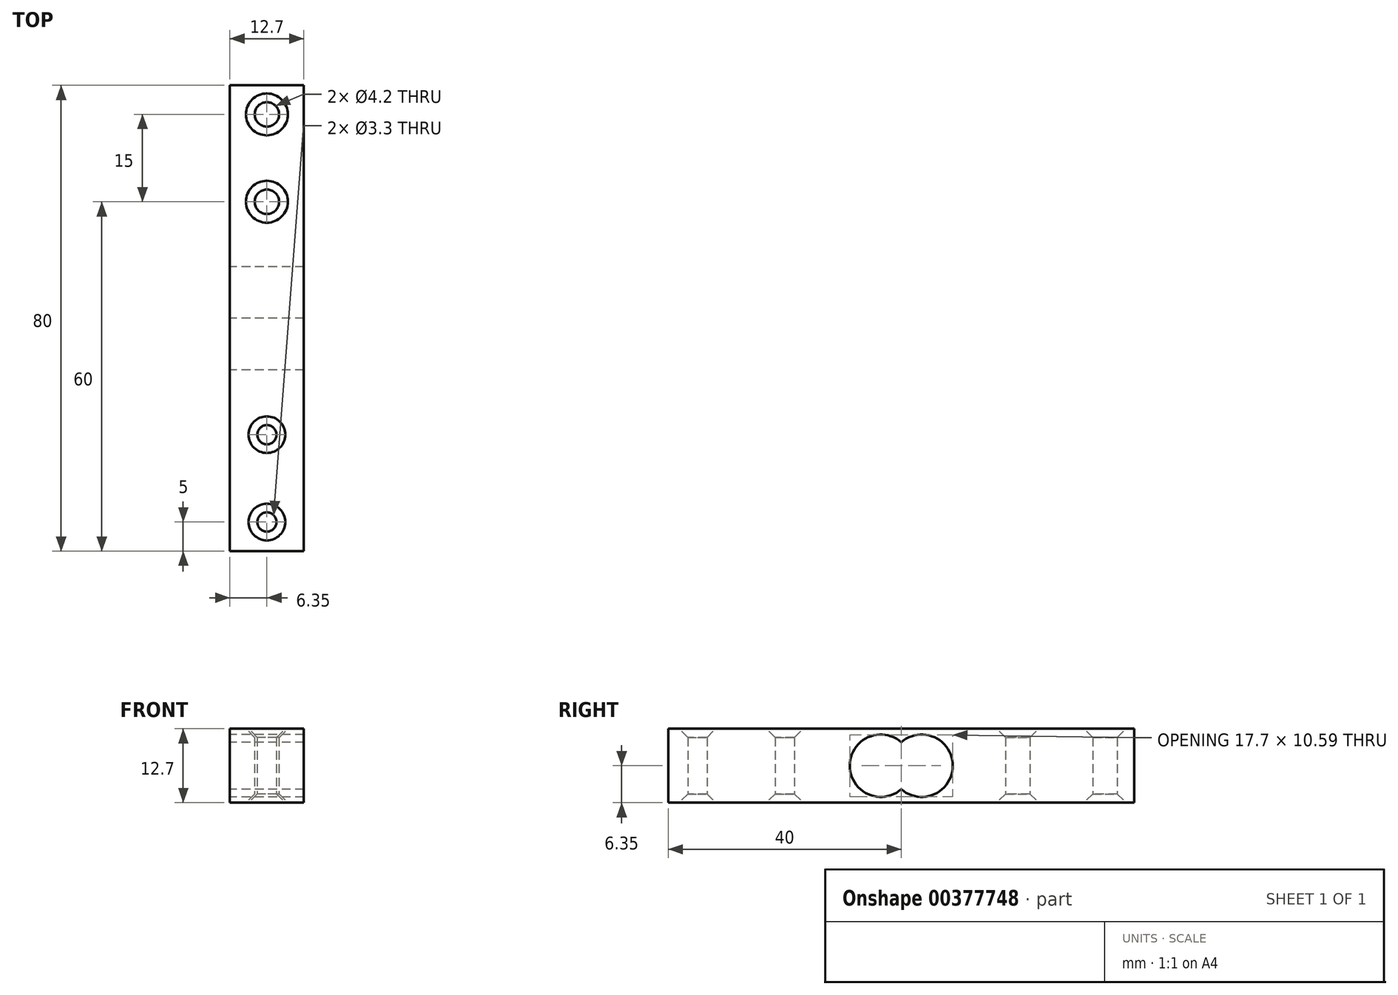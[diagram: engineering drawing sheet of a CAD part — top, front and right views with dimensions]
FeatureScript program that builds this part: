
annotation { "Feature Type Name" : "Feature", "Feature Type Description" : "" }
export const myFeature = defineFeature(function(context is Context, id is Id, definition is map)
    precondition{}
    {
        {
            var Q0;
            Q0=qCreatedBy(makeId("Top.planeOp"),FACE);
            var sketch = newSketch(context, id + "F0", { "sketchPlane" : qUnion([Q0])});
            skLineSegment(sketch, "E0.bottom", {"start": v(6.35, -40) * mm, "end": v(-6.35, -40) * mm});
            skLineSegment(sketch, "E0.top", {"start": v(6.35, 40) * mm, "end": v(-6.35, 40) * mm});
            skLineSegment(sketch, "E0.left", {"start": v(6.35, -40) * mm, "end": v(6.35, 40) * mm});
            skLineSegment(sketch, "E0.right", {"start": v(-6.35, -40) * mm, "end": v(-6.35, 40) * mm});
            skPoint(sketch, "E0.middle", {"position": v(0, 0) * mm});
            skLineSegment(sketch, "E1", {"start": v(0, 0) * mm, "end": v(0, 20) * mm, "construction": true});
            skLineSegment(sketch, "E2.MirrorCS", {"start": v(0, 0) * mm, "end": v(0, -20) * mm, "construction": true});
            skLineSegment(sketch, "E3", {"start": v(0, 20) * mm, "end": v(0, 35) * mm, "construction": true});
            skLineSegment(sketch, "E4.MirrorCS", {"start": v(0, -20) * mm, "end": v(0, -35) * mm, "construction": true});
            skCircle(sketch, "E5", {"center": v(0, 20) * mm, "radius": 2.1 * mm});
            skCircle(sketch, "E6", {"center": v(0, 35) * mm, "radius": 2.1 * mm});
            skCircle(sketch, "E7", {"center": v(0, -20) * mm, "radius": 1.65 * mm});
            skCircle(sketch, "E8", {"center": v(0, -35) * mm, "radius": 1.65 * mm});
            skSolve(sketch);
        }
        {
            var Q0;
            Q0 = qSketchRegion(id + "F0", true);
            extrude(context, id + "F1", {"entities" : qUnion([Q0]), "depth" : 12.7 * mm});
        }
        {
            var Q0;
            Q0=makeQuery(id+"F1.opExtrude","SWEPT_FACE",FACE,{"disambiguationData":[OSD([sQuery(id+"F0.wireOp",EDGE,"E0.right")])]});
            var sketch = newSketch(context, id + "F2", { "sketchPlane" : qUnion([Q0])});
            skLineSegment(sketch, "E9", {"start": v(0, 12.7) * mm, "end": v(0, 0) * mm, "construction": true});
            skLineSegment(sketch, "E10", {"start": v(0, 6.35) * mm, "end": v(-3.5, 6.35) * mm, "construction": true});
            skLineSegment(sketch, "E11.MirrorCS", {"start": v(0, 6.35) * mm, "end": v(3.5, 6.35) * mm, "construction": true});
            skCircle(sketch, "E12", {"center": v(-3.5, 6.35) * mm, "radius": 5.35 * mm});
            skCircle(sketch, "E13", {"center": v(3.5, 6.35) * mm, "radius": 5.35 * mm});
            skSolve(sketch);
        }
        {
            var Q0;
            {var subQ0=sQuery(id+"F2.wireOp",EDGE,"E13");var subQ1=sQuery(id+"F2.wireOp",EDGE,"E12");var subQ2=makeQuery(id+"F2.imprint","INTERSECT",VERTEX,{"disambiguationData":[OD(0.0)],"derivedFrom":[subQ1,subQ0]});Q0=makeQuery(id+"F2.imprint","IMPRINT",FACE,{"disambiguationData":[TD([[makeQuery(id+"F2.imprint","IMPRINT",EDGE,{"disambiguationData":[TD([[subQ2,1.0]])],"derivedFrom":subQ1}),1.0]])]});}
            var Q1;
            {var subQ0=sQuery(id+"F2.wireOp",EDGE,"E13");var subQ1=sQuery(id+"F2.wireOp",EDGE,"E12");var subQ2=makeQuery(id+"F2.imprint","INTERSECT",VERTEX,{"disambiguationData":[OD(0.0)],"derivedFrom":[subQ1,subQ0]});Q1=makeQuery(id+"F2.imprint","IMPRINT",FACE,{"disambiguationData":[TD([[makeQuery(id+"F2.imprint","IMPRINT",EDGE,{"disambiguationData":[TD([[subQ2,-1.0]])],"derivedFrom":subQ1}),-1.0]])]});}
            var Q2;
            {var subQ0=sQuery(id+"F2.wireOp",EDGE,"E13");var subQ1=sQuery(id+"F2.wireOp",EDGE,"E12");var subQ2=makeQuery(id+"F2.imprint","INTERSECT",VERTEX,{"disambiguationData":[OD(0.0)],"derivedFrom":[subQ1,subQ0]});Q2=makeQuery(id+"F2.imprint","IMPRINT",FACE,{"disambiguationData":[TD([[makeQuery(id+"F2.imprint","IMPRINT",EDGE,{"disambiguationData":[TD([[subQ2,-1.0]])],"derivedFrom":subQ1}),1.0]])]});}
            extrude(context, id + "F3", {"entities" : qUnion([Q0, Q1, Q2]), "operationType" : NewBodyOperationType.REMOVE, "endBound" : BoundingType.THROUGH_ALL, "oppositeDirection" : true, "depth" : 25 * mm});
        }
        {
            var Q0;
            Q0=makeQuery(id+"F1.opExtrude","CAP_EDGE",EDGE,{"disambiguationData":[OSD([sQuery(id+"F0.wireOp",EDGE,"E6")])],"isStart":false});
            var Q1;
            Q1=makeQuery(id+"F1.opExtrude","CAP_EDGE",EDGE,{"disambiguationData":[OSD([sQuery(id+"F0.wireOp",EDGE,"E5")])],"isStart":false});
            var Q2;
            Q2=makeQuery(id+"F1.opExtrude","CAP_EDGE",EDGE,{"disambiguationData":[OSD([sQuery(id+"F0.wireOp",EDGE,"E7")])],"isStart":false});
            var Q3;
            Q3=makeQuery(id+"F1.opExtrude","CAP_EDGE",EDGE,{"disambiguationData":[OSD([sQuery(id+"F0.wireOp",EDGE,"E8")])],"isStart":false});
            chamfer(context, id + "F4", {"entities" : qUnion([Q0, Q1, Q2, Q3]), "width" : 1.5 * mm, "tangentPropagation" : true});
        }
        {
            var Q0;
            Q0=makeQuery(id+"F1.opExtrude","CAP_EDGE",EDGE,{"disambiguationData":[OSD([sQuery(id+"F0.wireOp",EDGE,"E6")])],"isStart":true});
            var Q1;
            Q1=makeQuery(id+"F1.opExtrude","CAP_EDGE",EDGE,{"disambiguationData":[OSD([sQuery(id+"F0.wireOp",EDGE,"E5")])],"isStart":true});
            var Q2;
            Q2=makeQuery(id+"F1.opExtrude","CAP_EDGE",EDGE,{"disambiguationData":[OSD([sQuery(id+"F0.wireOp",EDGE,"E7")])],"isStart":true});
            var Q3;
            Q3=makeQuery(id+"F1.opExtrude","CAP_EDGE",EDGE,{"disambiguationData":[OSD([sQuery(id+"F0.wireOp",EDGE,"E8")])],"isStart":true});
            chamfer(context, id + "F5", {"entities" : qUnion([Q0, Q1, Q2, Q3]), "width" : 1.5 * mm, "tangentPropagation" : true});
        }
    });
